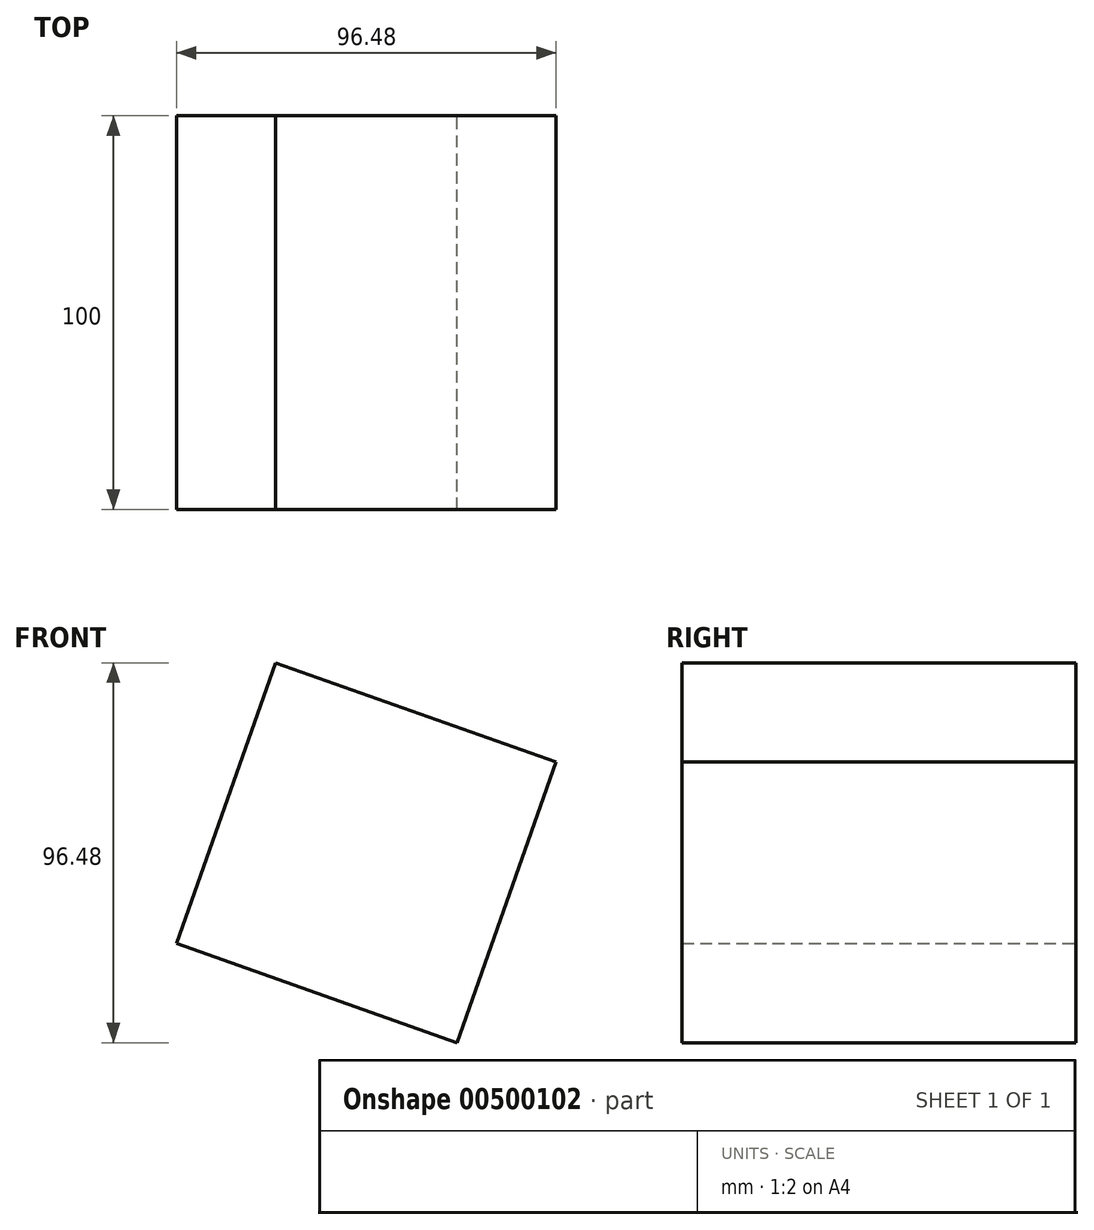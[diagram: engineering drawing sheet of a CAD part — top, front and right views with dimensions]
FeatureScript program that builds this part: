
annotation { "Feature Type Name" : "Feature", "Feature Type Description" : "" }
export const myFeature = defineFeature(function(context is Context, id is Id, definition is map)
    precondition{}
    {
        {
            var Q0;
            Q0=qCreatedBy(makeId("Front.planeOp"),FACE);
            var sketch = newSketch(context, id + "F0", { "sketchPlane" : qUnion([Q0])});
            skCircle(sketch, "E0.cCircle", {"center": v(0, 0) * mm, "radius": 53.45 * mm, "construction": true});
            skLineSegment(sketch, "E0.0", {"start": v(23.03, -48.24) * mm, "end": v(-48.24, -23.03) * mm});
            skLineSegment(sketch, "E0.1", {"start": v(-48.24, -23.03) * mm, "end": v(-23.03, 48.24) * mm});
            skLineSegment(sketch, "E0.2", {"start": v(-23.03, 48.24) * mm, "end": v(48.24, 23.03) * mm});
            skLineSegment(sketch, "E0.3", {"start": v(48.24, 23.03) * mm, "end": v(23.03, -48.24) * mm});
            skSolve(sketch);
        }
        {
            var Q0;
            Q0 = qSketchRegion(id + "F0", true);
            extrude(context, id + "F1", {"entities" : qUnion([Q0]), "endBound" : BoundingType.SYMMETRIC, "depth" : 100 * mm});
        }
    });
